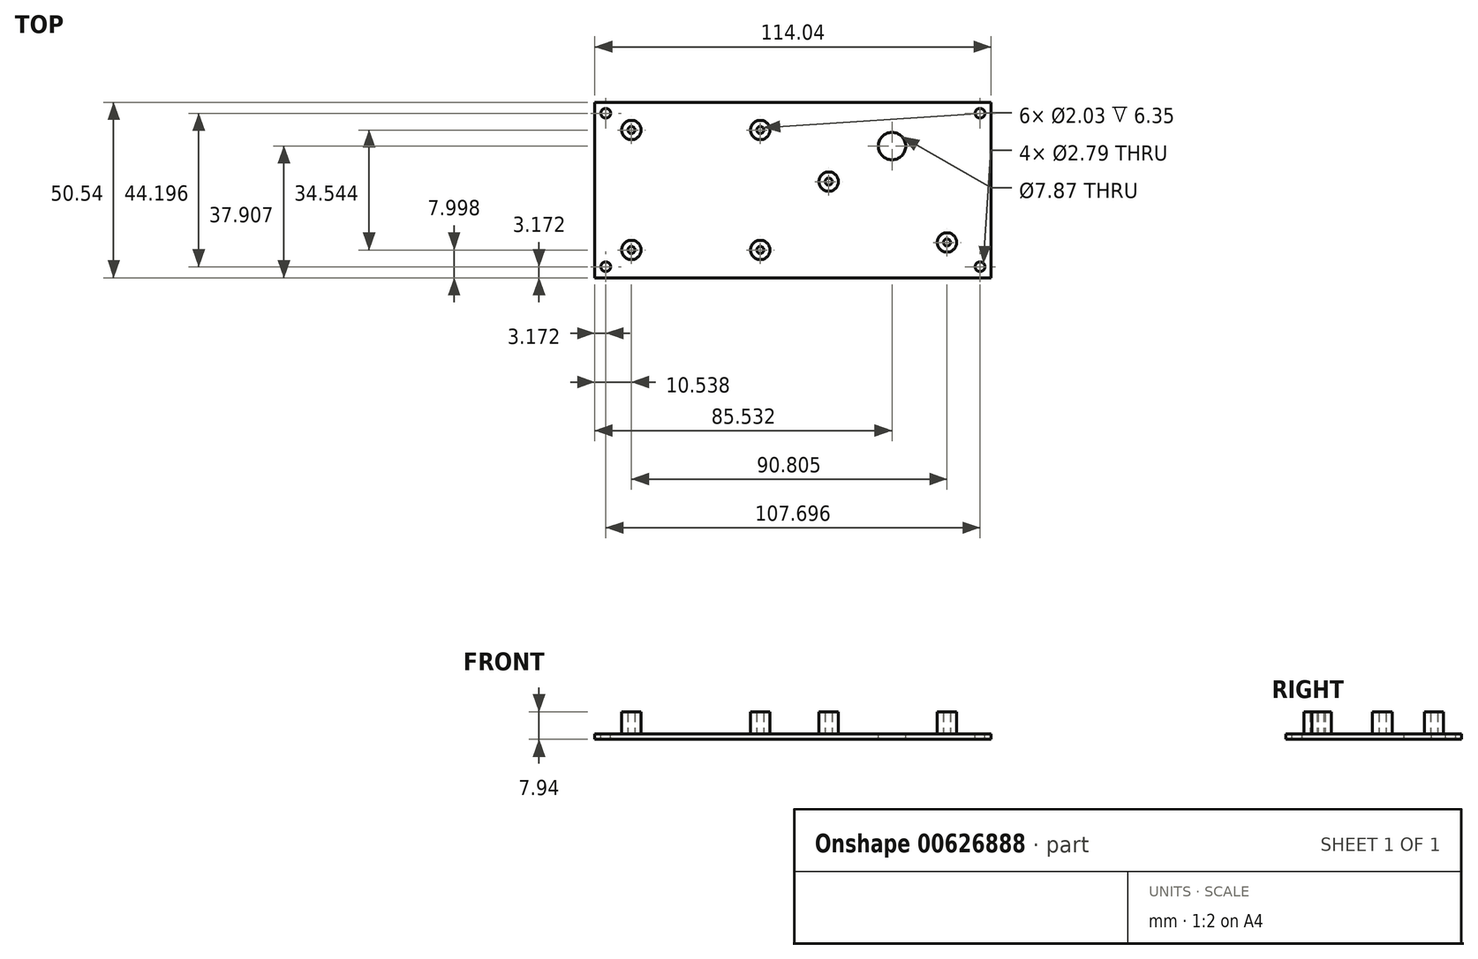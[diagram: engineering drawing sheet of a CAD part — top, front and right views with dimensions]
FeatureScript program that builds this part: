
annotation { "Feature Type Name" : "Feature", "Feature Type Description" : "" }
export const myFeature = defineFeature(function(context is Context, id is Id, definition is map)
    precondition{}
    {
        {
            var Q0;
            Q0=qCreatedBy(makeId("Top.planeOp"),FACE);
            var sketch = newSketch(context, id + "F0", { "sketchPlane" : qUnion([Q0])});
            skLineSegment(sketch, "E0.bottom", {"start": v(57.02, -25.27) * mm, "end": v(-57.02, -25.27) * mm});
            skLineSegment(sketch, "E0.top", {"start": v(57.02, 25.27) * mm, "end": v(-57.02, 25.27) * mm});
            skLineSegment(sketch, "E0.left", {"start": v(57.02, -25.27) * mm, "end": v(57.02, 25.27) * mm});
            skLineSegment(sketch, "E0.right", {"start": v(-57.02, -25.27) * mm, "end": v(-57.02, 25.27) * mm});
            skLineSegment(sketch, "E1.bottom", {"start": v(57.02, -25.27) * mm, "end": v(44.32, -25.27) * mm, "construction": true});
            skLineSegment(sketch, "E1.top", {"start": v(57.02, -15.11) * mm, "end": v(44.32, -15.11) * mm, "construction": true});
            skLineSegment(sketch, "E1.left", {"start": v(57.02, -25.27) * mm, "end": v(57.02, -15.11) * mm, "construction": true});
            skLineSegment(sketch, "E1.right", {"start": v(44.32, -25.27) * mm, "end": v(44.32, -15.11) * mm, "construction": true});
            skLineSegment(sketch, "E2.bottom", {"start": v(44.32, -17.9) * mm, "end": v(51.44, -17.9) * mm, "construction": true});
            skLineSegment(sketch, "E2.top", {"start": v(44.32, -15.11) * mm, "end": v(51.44, -15.11) * mm, "construction": true});
            skLineSegment(sketch, "E2.left", {"start": v(44.32, -17.9) * mm, "end": v(44.32, -15.11) * mm, "construction": true});
            skLineSegment(sketch, "E2.right", {"start": v(51.44, -17.9) * mm, "end": v(51.44, -15.11) * mm, "construction": true});
            skCircle(sketch, "E3", {"center": v(44.32, -15.11) * mm, "radius": 1.02 * mm});
            skCircle(sketch, "E4", {"center": v(44.32, -15.11) * mm, "radius": 2.8 * mm});
            skLineSegment(sketch, "E5.bottom", {"start": v(44.32, -15.11) * mm, "end": v(10.29, -15.11) * mm, "construction": true});
            skLineSegment(sketch, "E5.top", {"start": v(44.32, 2.41) * mm, "end": v(10.29, 2.41) * mm, "construction": true});
            skLineSegment(sketch, "E5.left", {"start": v(44.32, -15.11) * mm, "end": v(44.32, 2.41) * mm, "construction": true});
            skLineSegment(sketch, "E5.right", {"start": v(10.29, -15.11) * mm, "end": v(10.29, 2.41) * mm, "construction": true});
            skCircle(sketch, "E6", {"center": v(10.29, 2.41) * mm, "radius": 1.02 * mm});
            skCircle(sketch, "E7", {"center": v(10.29, 2.41) * mm, "radius": 2.8 * mm});
            skLineSegment(sketch, "E8.left", {"start": v(51.44, -17.9) * mm, "end": v(51.44, 5.72) * mm, "construction": true});
            skLineSegment(sketch, "E9.bottom", {"start": v(51.44, -17.9) * mm, "end": v(3.18, -17.9) * mm, "construction": true});
            skLineSegment(sketch, "E9.top", {"start": v(51.44, 5.2) * mm, "end": v(3.18, 5.2) * mm, "construction": true});
            skLineSegment(sketch, "E9.left", {"start": v(51.44, -17.9) * mm, "end": v(51.44, 5.2) * mm, "construction": true});
            skLineSegment(sketch, "E9.right", {"start": v(3.18, -17.9) * mm, "end": v(3.18, 5.2) * mm, "construction": true});
            skLineSegment(sketch, "E10.bottom", {"start": v(10.29, 2.41) * mm, "end": v(3.18, 2.41) * mm, "construction": true});
            skLineSegment(sketch, "E10.top", {"start": v(10.29, 5.2) * mm, "end": v(3.18, 5.2) * mm, "construction": true});
            skLineSegment(sketch, "E10.left", {"start": v(10.29, 2.41) * mm, "end": v(10.29, 5.2) * mm, "construction": true});
            skLineSegment(sketch, "E10.right", {"start": v(3.18, 2.41) * mm, "end": v(3.18, 5.2) * mm, "construction": true});
            skCircle(sketch, "E11", {"center": v(28.51, 12.64) * mm, "radius": 3.94 * mm});
            skLineSegment(sketch, "E12", {"start": v(0, 25.27) * mm, "end": v(0, -25.27) * mm, "construction": true});
            skLineSegment(sketch, "E13", {"start": v(-57.02, 0) * mm, "end": v(57.02, 0) * mm, "construction": true});
            skLineSegment(sketch, "E14", {"start": v(57.02, 25.27) * mm, "end": v(0, 0) * mm, "construction": true});
            skLineSegment(sketch, "E15.bottom", {"start": v(-9.4, 17.27) * mm, "end": v(-46.48, 17.27) * mm, "construction": true});
            skLineSegment(sketch, "E15.top", {"start": v(-9.4, -17.27) * mm, "end": v(-46.48, -17.27) * mm, "construction": true});
            skLineSegment(sketch, "E15.left", {"start": v(-9.4, 17.27) * mm, "end": v(-9.4, -17.27) * mm, "construction": true});
            skLineSegment(sketch, "E15.right", {"start": v(-46.48, 17.27) * mm, "end": v(-46.48, -17.27) * mm, "construction": true});
            skPoint(sketch, "E15.middle", {"position": v(-27.94, 0) * mm});
            skCircle(sketch, "E16", {"center": v(-9.4, 17.27) * mm, "radius": 1.02 * mm});
            skCircle(sketch, "E17", {"center": v(-9.4, 17.27) * mm, "radius": 2.8 * mm});
            skCircle(sketch, "E18", {"center": v(-9.4, -17.27) * mm, "radius": 1.02 * mm});
            skCircle(sketch, "E19", {"center": v(-9.4, -17.27) * mm, "radius": 2.8 * mm});
            skCircle(sketch, "E20", {"center": v(-46.48, 17.27) * mm, "radius": 1.02 * mm});
            skCircle(sketch, "E21", {"center": v(-46.48, 17.27) * mm, "radius": 2.8 * mm});
            skCircle(sketch, "E22", {"center": v(-46.48, -17.27) * mm, "radius": 1.02 * mm});
            skCircle(sketch, "E23", {"center": v(-46.48, -17.27) * mm, "radius": 2.8 * mm});
            skLineSegment(sketch, "E24.bottom", {"start": v(57.02, 25.27) * mm, "end": v(53.85, 25.27) * mm});
            skLineSegment(sketch, "E24.top", {"start": v(57.02, 22.1) * mm, "end": v(53.85, 22.1) * mm, "construction": true});
            skLineSegment(sketch, "E24.left", {"start": v(57.02, 25.27) * mm, "end": v(57.02, 22.1) * mm});
            skLineSegment(sketch, "E24.right", {"start": v(53.85, 25.27) * mm, "end": v(53.85, 22.1) * mm, "construction": true});
            skLineSegment(sketch, "E25.bottom", {"start": v(57.02, -25.27) * mm, "end": v(53.85, -25.27) * mm});
            skLineSegment(sketch, "E25.top", {"start": v(57.02, -22.1) * mm, "end": v(53.85, -22.1) * mm, "construction": true});
            skLineSegment(sketch, "E25.left", {"start": v(57.02, -25.27) * mm, "end": v(57.02, -22.1) * mm});
            skLineSegment(sketch, "E25.right", {"start": v(53.85, -25.27) * mm, "end": v(53.85, -22.1) * mm, "construction": true});
            skLineSegment(sketch, "E26.bottom", {"start": v(-57.02, 25.27) * mm, "end": v(-53.85, 25.27) * mm});
            skLineSegment(sketch, "E26.top", {"start": v(-57.02, 22.1) * mm, "end": v(-53.85, 22.1) * mm, "construction": true});
            skLineSegment(sketch, "E26.left", {"start": v(-57.02, 25.27) * mm, "end": v(-57.02, 22.1) * mm});
            skLineSegment(sketch, "E26.right", {"start": v(-53.85, 25.27) * mm, "end": v(-53.85, 22.1) * mm, "construction": true});
            skLineSegment(sketch, "E27.bottom", {"start": v(-57.02, -25.27) * mm, "end": v(-53.85, -25.27) * mm});
            skLineSegment(sketch, "E27.top", {"start": v(-57.02, -22.1) * mm, "end": v(-53.85, -22.1) * mm, "construction": true});
            skLineSegment(sketch, "E27.left", {"start": v(-57.02, -25.27) * mm, "end": v(-57.02, -22.1) * mm});
            skLineSegment(sketch, "E27.right", {"start": v(-53.85, -25.27) * mm, "end": v(-53.85, -22.1) * mm, "construction": true});
            skCircle(sketch, "E28", {"center": v(-53.85, 22.1) * mm, "radius": 1.4 * mm});
            skCircle(sketch, "E29", {"center": v(53.85, 22.1) * mm, "radius": 1.4 * mm});
            skCircle(sketch, "E30", {"center": v(53.85, -22.1) * mm, "radius": 1.4 * mm});
            skCircle(sketch, "E31", {"center": v(-53.85, -22.1) * mm, "radius": 1.4 * mm});
            skSolve(sketch);
        }
        {
            var Q0;
            Q0=makeQuery(id+"F0.imprint","IMPRINT",FACE,{"disambiguationData":[TD([[makeQuery(id+"F0.imprint","IMPRINT",EDGE,{"derivedFrom":sQuery(id+"F0.wireOp",EDGE,"E0.bottom")}),-1.0]])]});
            var Q1;
            Q1=makeQuery(id+"F0.imprint","IMPRINT",FACE,{"disambiguationData":[TD([[makeQuery(id+"F0.imprint","IMPRINT",EDGE,{"derivedFrom":sQuery(id+"F0.wireOp",EDGE,"E16")}),-1.0]])]});
            var Q2;
            Q2=makeQuery(id+"F0.imprint","IMPRINT",FACE,{"disambiguationData":[TD([[makeQuery(id+"F0.imprint","IMPRINT",EDGE,{"derivedFrom":sQuery(id+"F0.wireOp",EDGE,"E16")}),1.0]])]});
            var Q3;
            Q3=makeQuery(id+"F0.imprint","IMPRINT",FACE,{"disambiguationData":[TD([[makeQuery(id+"F0.imprint","IMPRINT",EDGE,{"derivedFrom":sQuery(id+"F0.wireOp",EDGE,"E18")}),1.0]])]});
            var Q4;
            Q4=makeQuery(id+"F0.imprint","IMPRINT",FACE,{"disambiguationData":[TD([[makeQuery(id+"F0.imprint","IMPRINT",EDGE,{"derivedFrom":sQuery(id+"F0.wireOp",EDGE,"E18")}),-1.0]])]});
            var Q5;
            Q5=makeQuery(id+"F0.imprint","IMPRINT",FACE,{"disambiguationData":[TD([[makeQuery(id+"F0.imprint","IMPRINT",EDGE,{"derivedFrom":sQuery(id+"F0.wireOp",EDGE,"E22")}),-1.0]])]});
            var Q6;
            Q6=makeQuery(id+"F0.imprint","IMPRINT",FACE,{"disambiguationData":[TD([[makeQuery(id+"F0.imprint","IMPRINT",EDGE,{"derivedFrom":sQuery(id+"F0.wireOp",EDGE,"E22")}),1.0]])]});
            var Q7;
            Q7=makeQuery(id+"F0.imprint","IMPRINT",FACE,{"disambiguationData":[TD([[makeQuery(id+"F0.imprint","IMPRINT",EDGE,{"derivedFrom":sQuery(id+"F0.wireOp",EDGE,"E20")}),-1.0]])]});
            var Q8;
            Q8=makeQuery(id+"F0.imprint","IMPRINT",FACE,{"disambiguationData":[TD([[makeQuery(id+"F0.imprint","IMPRINT",EDGE,{"derivedFrom":sQuery(id+"F0.wireOp",EDGE,"E20")}),1.0]])]});
            var Q9;
            Q9=makeQuery(id+"F0.imprint","IMPRINT",FACE,{"disambiguationData":[TD([[makeQuery(id+"F0.imprint","IMPRINT",EDGE,{"derivedFrom":sQuery(id+"F0.wireOp",EDGE,"E6")}),-1.0]])]});
            var Q10;
            Q10=makeQuery(id+"F0.imprint","IMPRINT",FACE,{"disambiguationData":[TD([[makeQuery(id+"F0.imprint","IMPRINT",EDGE,{"derivedFrom":sQuery(id+"F0.wireOp",EDGE,"E6")}),1.0]])]});
            var Q11;
            Q11=makeQuery(id+"F0.imprint","IMPRINT",FACE,{"disambiguationData":[TD([[makeQuery(id+"F0.imprint","IMPRINT",EDGE,{"derivedFrom":sQuery(id+"F0.wireOp",EDGE,"E3")}),-1.0]])]});
            var Q12;
            Q12=makeQuery(id+"F0.imprint","IMPRINT",FACE,{"disambiguationData":[TD([[makeQuery(id+"F0.imprint","IMPRINT",EDGE,{"derivedFrom":sQuery(id+"F0.wireOp",EDGE,"E3")}),1.0]])]});
            extrude(context, id + "F1", {"entities" : qUnion([Q0, Q1, Q2, Q3, Q4, Q5, Q6, Q7, Q8, Q9, Q10, Q11, Q12]), "oppositeDirection" : true, "depth" : 1.59 * mm, "offsetDistance" : 25.4 * mm});
        }
        {
            var Q0;
            Q0=makeQuery(id+"F0.imprint","IMPRINT",FACE,{"disambiguationData":[TD([[makeQuery(id+"F0.imprint","IMPRINT",EDGE,{"derivedFrom":sQuery(id+"F0.wireOp",EDGE,"E6")}),-1.0]])]});
            var Q1;
            Q1=makeQuery(id+"F0.imprint","IMPRINT",FACE,{"disambiguationData":[TD([[makeQuery(id+"F0.imprint","IMPRINT",EDGE,{"derivedFrom":sQuery(id+"F0.wireOp",EDGE,"E3")}),-1.0]])]});
            var Q2;
            Q2=makeQuery(id+"F0.imprint","IMPRINT",FACE,{"disambiguationData":[TD([[makeQuery(id+"F0.imprint","IMPRINT",EDGE,{"derivedFrom":sQuery(id+"F0.wireOp",EDGE,"E18")}),-1.0]])]});
            var Q3;
            Q3=makeQuery(id+"F0.imprint","IMPRINT",FACE,{"disambiguationData":[TD([[makeQuery(id+"F0.imprint","IMPRINT",EDGE,{"derivedFrom":sQuery(id+"F0.wireOp",EDGE,"E16")}),-1.0]])]});
            var Q4;
            Q4=makeQuery(id+"F0.imprint","IMPRINT",FACE,{"disambiguationData":[TD([[makeQuery(id+"F0.imprint","IMPRINT",EDGE,{"derivedFrom":sQuery(id+"F0.wireOp",EDGE,"E20")}),-1.0]])]});
            var Q5;
            Q5=makeQuery(id+"F0.imprint","IMPRINT",FACE,{"disambiguationData":[TD([[makeQuery(id+"F0.imprint","IMPRINT",EDGE,{"derivedFrom":sQuery(id+"F0.wireOp",EDGE,"E22")}),-1.0]])]});
            extrude(context, id + "F2", {"entities" : qUnion([Q0, Q1, Q2, Q3, Q4, Q5]), "operationType" : NewBodyOperationType.ADD, "depth" : 6.35 * mm, "offsetDistance" : 25.4 * mm});
        }
    });
